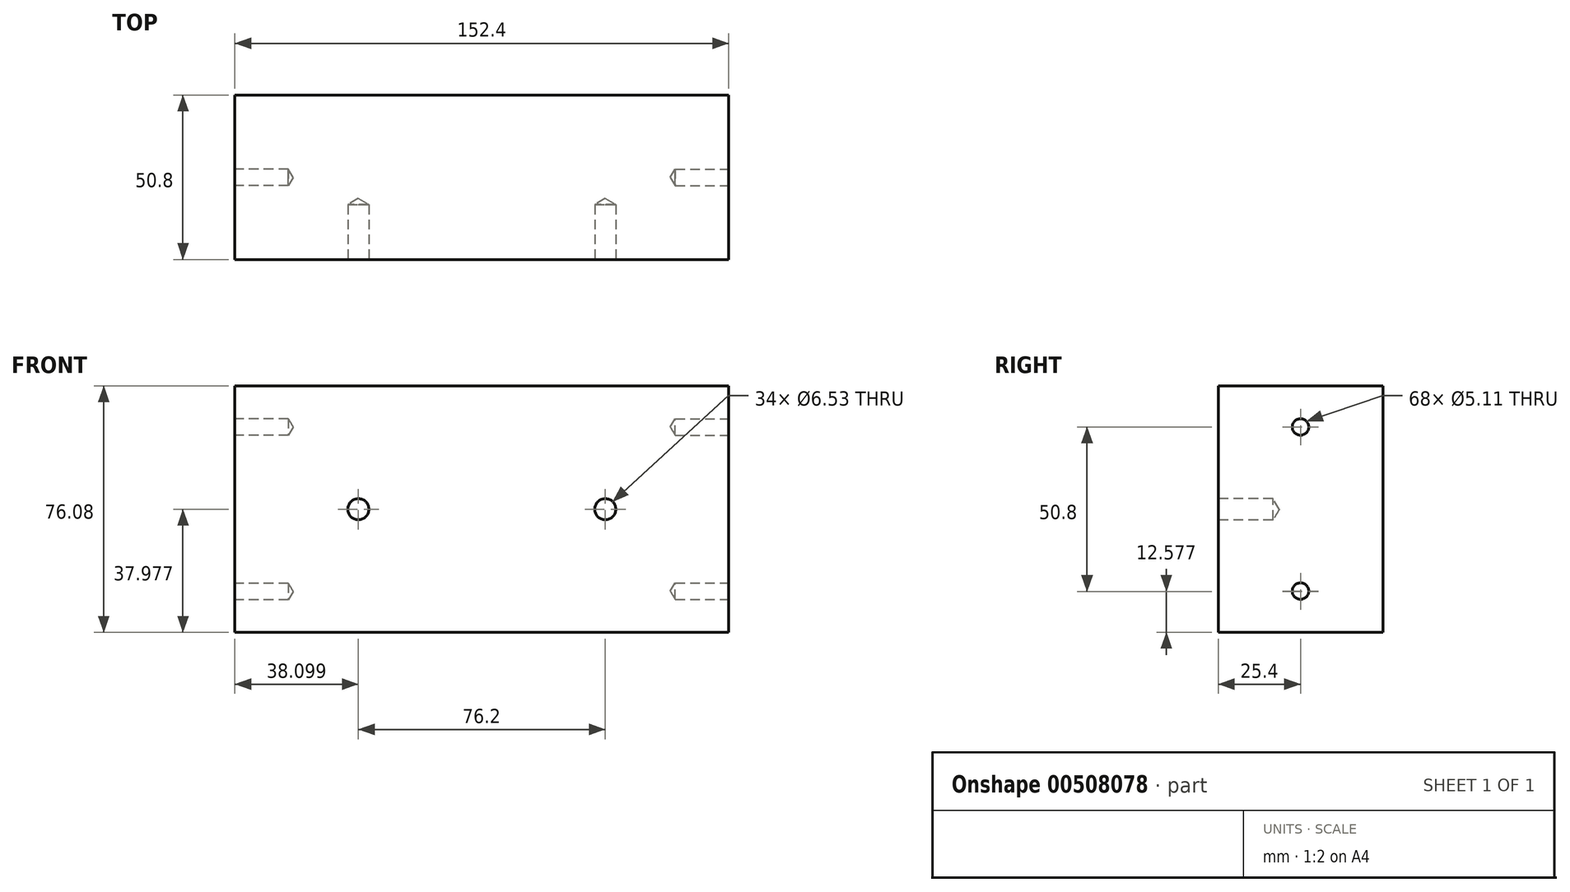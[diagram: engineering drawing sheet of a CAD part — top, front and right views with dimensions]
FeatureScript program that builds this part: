
annotation { "Feature Type Name" : "Feature", "Feature Type Description" : "" }
export const myFeature = defineFeature(function(context is Context, id is Id, definition is map)
    precondition{}
    {
        {
            var Q0;
            Q0=qCreatedBy(makeId("Front.planeOp"),FACE);
            var sketch = newSketch(context, id + "F0", { "sketchPlane" : qUnion([Q0])});
            skLineSegment(sketch, "E0.bottom", {"start": v(-76.31, 69.43) * mm, "end": v(76.09, 69.43) * mm});
            skLineSegment(sketch, "E0.top", {"start": v(-76.31, -6.65) * mm, "end": v(76.09, -6.65) * mm});
            skLineSegment(sketch, "E0.left", {"start": v(-76.31, 69.43) * mm, "end": v(-76.31, -6.65) * mm});
            skLineSegment(sketch, "E0.right", {"start": v(76.09, 69.43) * mm, "end": v(76.09, -6.65) * mm});
            skSolve(sketch);
        }
        {
            var Q0;
            Q0 = qSketchRegion(id + "F0", true);
            extrude(context, id + "F1", {"entities" : qUnion([Q0]), "depth" : 50.8 * mm});
        }
        {
            var Q0;
            Q0=makeQuery(id+"F1.opExtrude","SWEPT_FACE",FACE,{"disambiguationData":[OSD([sQuery(id+"F0.wireOp",EDGE,"E0.left")])]});
            var sketch = newSketch(context, id + "F2", { "sketchPlane" : qUnion([Q0])});
            skPoint(sketch, "E1", {"position": v(25.4, 56.73) * mm});
            skPoint(sketch, "E2", {"position": v(25.4, 5.93) * mm});
            skSolve(sketch);
        }
        {
            var Q0;
            Q0=sQuery(id+"F2.wireOp",VERTEX,"E1");
            var Q1;
            Q1=sQuery(id+"F2.wireOp",VERTEX,"E2");
            var Q2;
            Q2=makeQuery(id+"F1.opExtrude","SWEPT_BODY",BODY,{"disambiguationData":[OSD([sQuery(id+"F0.wireOp",EDGE,"E0.bottom"),sQuery(id+"F0.wireOp",EDGE,"E0.top"),sQuery(id+"F0.wireOp",EDGE,"E0.left"),sQuery(id+"F0.wireOp",EDGE,"E0.right")])]});
            hole(context, id + "F3", {"style" : HoleStyle.SIMPLE, "endStyle" : HoleEndStyle.BLIND, "standardTappedOrClearance" : lookupTablePath({ "standard" : "ANSI", "engagement" : "75%", "pitch" : "20 tpi", "size" : "1/4", "type" : "Tapped" }), "standardBlindInLast" : lookupTablePath({ "standard" : "ANSI", "engagement" : "75%", "pitch" : "20 tpi", "size" : "1/4", "type" : "Tapped" }), "holeDiameter" : 5.1 * mm, "showTappedDepth" : true, "holeDepth" : 16.5 * mm, "isTappedThrough" : true, "tappedDepth" : 12.7 * mm, "tapClearance" : 3, "startFromSketch" : true, "locations" : qUnion([Q0, Q1]), "scope" : qUnion([Q2]), "majorDiameter" : 6.35 * mm});
        }
        {
            var Q0;
            Q0=makeQuery(id+"F1.opExtrude","SWEPT_FACE",FACE,{"disambiguationData":[OSD([sQuery(id+"F0.wireOp",EDGE,"E0.right")])]});
            var sketch = newSketch(context, id + "F4", { "sketchPlane" : qUnion([Q0])});
            skPoint(sketch, "E3", {"position": v(-25.4, 56.73) * mm});
            skPoint(sketch, "E4", {"position": v(-25.4, 6.05) * mm});
            skSolve(sketch);
        }
        {
            var Q0;
            Q0=sQuery(id+"F4.wireOp",VERTEX,"E3");
            var Q1;
            Q1=sQuery(id+"F4.wireOp",VERTEX,"E4");
            var Q2;
            Q2=makeQuery(id+"F1.opExtrude","SWEPT_BODY",BODY,{"disambiguationData":[OSD([sQuery(id+"F0.wireOp",EDGE,"E0.bottom"),sQuery(id+"F0.wireOp",EDGE,"E0.top"),sQuery(id+"F0.wireOp",EDGE,"E0.left"),sQuery(id+"F0.wireOp",EDGE,"E0.right")])]});
            hole(context, id + "F5", {"style" : HoleStyle.SIMPLE, "endStyle" : HoleEndStyle.BLIND, "standardTappedOrClearance" : lookupTablePath({ "standard" : "ANSI", "engagement" : "75%", "pitch" : "20 tpi", "size" : "1/4", "type" : "Tapped" }), "standardBlindInLast" : lookupTablePath({ "standard" : "ANSI", "engagement" : "75%", "pitch" : "20 tpi", "size" : "1/4", "type" : "Tapped" }), "holeDiameter" : 5.1 * mm, "showTappedDepth" : true, "holeDepth" : 16.5 * mm, "isTappedThrough" : true, "tappedDepth" : 12.7 * mm, "tapClearance" : 3, "startFromSketch" : true, "locations" : qUnion([Q0, Q1]), "scope" : qUnion([Q2]), "majorDiameter" : 6.35 * mm});
        }
        {
            var Q0;
            Q0=makeQuery(id+"F1.opExtrude","CAP_FACE",FACE,{"disambiguationData":[OSD([sQuery(id+"F0.wireOp",EDGE,"E0.bottom"),sQuery(id+"F0.wireOp",EDGE,"E0.top"),sQuery(id+"F0.wireOp",EDGE,"E0.left"),sQuery(id+"F0.wireOp",EDGE,"E0.right")])],"isStart":false});
            var sketch = newSketch(context, id + "F6", { "sketchPlane" : qUnion([Q0])});
            skPoint(sketch, "E5", {"position": v(-38.21, 31.33) * mm});
            skPoint(sketch, "E6", {"position": v(37.99, 31.33) * mm});
            skSolve(sketch);
        }
        {
            var Q0;
            Q0=sQuery(id+"F6.wireOp",VERTEX,"E5");
            var Q1;
            Q1=sQuery(id+"F6.wireOp",VERTEX,"E6");
            var Q2;
            Q2=makeQuery(id+"F1.opExtrude","SWEPT_BODY",BODY,{"disambiguationData":[OSD([sQuery(id+"F0.wireOp",EDGE,"E0.bottom"),sQuery(id+"F0.wireOp",EDGE,"E0.top"),sQuery(id+"F0.wireOp",EDGE,"E0.left"),sQuery(id+"F0.wireOp",EDGE,"E0.right")])]});
            hole(context, id + "F7", {"style" : HoleStyle.SIMPLE, "endStyle" : HoleEndStyle.BLIND, "standardTappedOrClearance" : lookupTablePath({ "standard" : "ANSI", "engagement" : "75%", "pitch" : "18 tpi", "size" : "5/16", "type" : "Tapped" }), "standardBlindInLast" : lookupTablePath({ "standard" : "ANSI", "engagement" : "75%", "pitch" : "18 tpi", "size" : "5/16", "type" : "Tapped" }), "holeDiameter" : 6.53 * mm, "showTappedDepth" : true, "holeDepth" : 16.93 * mm, "isTappedThrough" : true, "tappedDepth" : 12.7 * mm, "tapClearance" : 3, "startFromSketch" : true, "locations" : qUnion([Q0, Q1]), "scope" : qUnion([Q2]), "majorDiameter" : 7.94 * mm});
        }
    });
